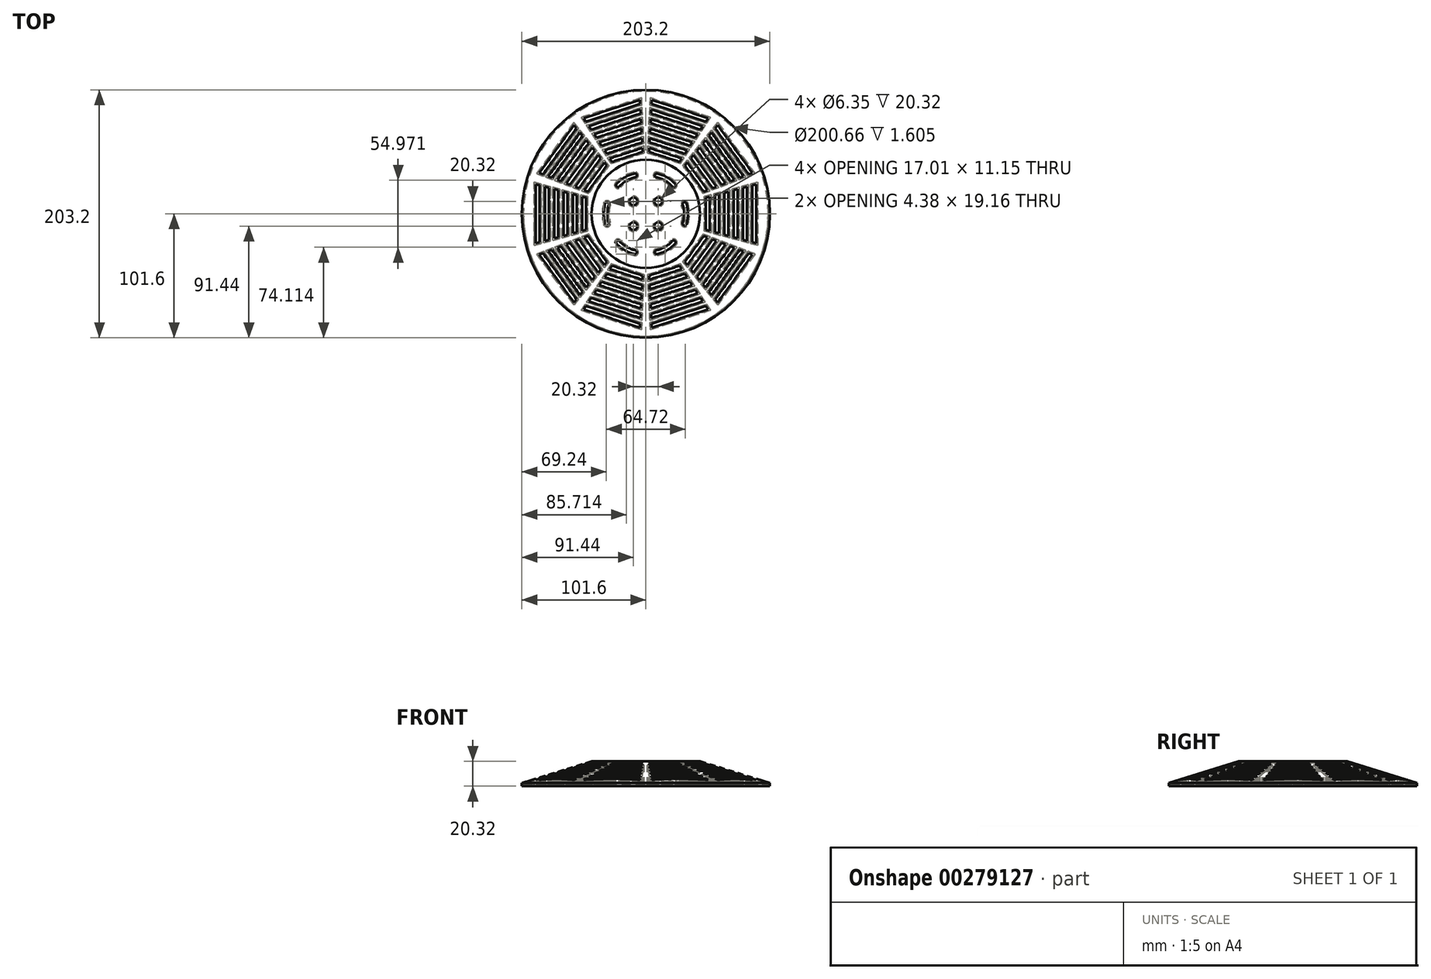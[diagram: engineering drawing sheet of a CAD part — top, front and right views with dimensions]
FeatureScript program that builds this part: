
annotation { "Feature Type Name" : "Feature", "Feature Type Description" : "" }
export const myFeature = defineFeature(function(context is Context, id is Id, definition is map)
    precondition{}
    {
        {
            var Q0;
            Q0=qCreatedBy(makeId("Front.planeOp"),FACE);
            var sketch = newSketch(context, id + "F0", { "sketchPlane" : qUnion([Q0])});
            skLineSegment(sketch, "E0", {"start": v(0, 0) * mm, "end": v(0, 20.32) * mm});
            skLineSegment(sketch, "E1", {"start": v(0, 20.32) * mm, "end": v(44.45, 20.32) * mm});
            skLineSegment(sketch, "E2", {"start": v(44.45, 20.32) * mm, "end": v(101.6, 2.54) * mm});
            skLineSegment(sketch, "E3", {"start": v(101.6, 2.54) * mm, "end": v(101.6, 0) * mm});
            skLineSegment(sketch, "E4", {"start": v(101.6, 0) * mm, "end": v(0, 0) * mm});
            skSolve(sketch);
        }
        {
            var Q0;
            Q0=makeQuery(id+"F0.imprint","IMPRINT",FACE,{"disambiguationData":[TD([[makeQuery(id+"F0.imprint","IMPRINT",EDGE,{"derivedFrom":sQuery(id+"F0.wireOp",EDGE,"E0")}),-1.0]])]});
            var Q1;
            Q1=sQuery(id+"F0.wireOp",EDGE,"E0");
            revolve(context, id + "F1", {"entities" : qUnion([Q0]), "axis" : qUnion([Q1]), "revolveType" : RevolveType.FULL});
        }
        {
            var Q0;
            Q0=makeQuery(id+"F1.opRevolve","SWEPT_FACE",FACE,{"disambiguationData":[OSD([sQuery(id+"F0.wireOp",EDGE,"E1")])]});
            var sketch = newSketch(context, id + "F2", { "sketchPlane" : qUnion([Q0])});
            skArc(sketch, "E5", {"start": v(-30.23, 7.53) * mm, "mid": v(-31.38, 0) * mm, "end": v(-30.23, -7.53) * mm});
            skArc(sketch, "E6.0", {"start": v(-33.27, 8.47) * mm, "mid": v(-34.55, 0) * mm, "end": v(-33.27, -8.47) * mm});
            skArc(sketch, "E7", {"start": v(-33.27, -8.47) * mm, "mid": v(-31.28, -9.52) * mm, "end": v(-30.23, -7.53) * mm});
            skArc(sketch, "E8", {"start": v(-30.23, 7.53) * mm, "mid": v(-31.28, 9.52) * mm, "end": v(-33.27, 8.47) * mm});
            skSolve(sketch);
        }
        {
            var Q0;
            Q0=makeQuery(id+"F2.imprint","IMPRINT",FACE,{"disambiguationData":[TD([[makeQuery(id+"F2.imprint","IMPRINT",EDGE,{"derivedFrom":sQuery(id+"F2.wireOp",EDGE,"E5")}),-1.0]])]});
            extrude(context, id + "F3", {"entities" : qUnion([Q0]), "endBound" : BoundingType.THROUGH_ALL, "oppositeDirection" : true, "depth" : 25.4 * mm});
        }
        {
            var Q0;
            Q0=makeQuery(id+"F3.opExtrude","SWEPT_BODY",BODY,{"disambiguationData":[OSD([sQuery(id+"F2.wireOp",EDGE,"E5"),sQuery(id+"F2.wireOp",EDGE,"E6.0"),sQuery(id+"F2.wireOp",EDGE,"E7"),sQuery(id+"F2.wireOp",EDGE,"E8")])]});
            var Q1;
            Q1=makeQuery(id+"F1.opRevolve","SWEPT_EDGE",EDGE,{"disambiguationData":[OSD([sQuery(id+"F0.wireOp",EDGE,"E2"),sQuery(id+"F0.wireOp",EDGE,"E3")])]});
            circularPattern(context, id + "F4", {"entities" : qUnion([Q0]), "axis" : qUnion([Q1]), "angle" : 360 * degree, "instanceCount" : 6, "equalSpace" : true});
        }
        {
            var Q0;
            Q0=makeQuery(id+"F3.opExtrude","SWEPT_BODY",BODY,{"disambiguationData":[OSD([sQuery(id+"F2.wireOp",EDGE,"E5"),sQuery(id+"F2.wireOp",EDGE,"E6.0"),sQuery(id+"F2.wireOp",EDGE,"E7"),sQuery(id+"F2.wireOp",EDGE,"E8")])]});
            var Q1;
            Q1=makeQuery(id+"F4.opPattern","COPY",BODY,{"derivedFrom":makeQuery(id+"F3.opExtrude","SWEPT_BODY",BODY,{"disambiguationData":[OSD([sQuery(id+"F2.wireOp",EDGE,"E5"),sQuery(id+"F2.wireOp",EDGE,"E6.0"),sQuery(id+"F2.wireOp",EDGE,"E7"),sQuery(id+"F2.wireOp",EDGE,"E8")])]}),"instanceName":"1"});
            var Q2;
            Q2=makeQuery(id+"F4.opPattern","COPY",BODY,{"derivedFrom":makeQuery(id+"F3.opExtrude","SWEPT_BODY",BODY,{"disambiguationData":[OSD([sQuery(id+"F2.wireOp",EDGE,"E5"),sQuery(id+"F2.wireOp",EDGE,"E6.0"),sQuery(id+"F2.wireOp",EDGE,"E7"),sQuery(id+"F2.wireOp",EDGE,"E8")])]}),"instanceName":"2"});
            var Q3;
            Q3=makeQuery(id+"F4.opPattern","COPY",BODY,{"derivedFrom":makeQuery(id+"F3.opExtrude","SWEPT_BODY",BODY,{"disambiguationData":[OSD([sQuery(id+"F2.wireOp",EDGE,"E5"),sQuery(id+"F2.wireOp",EDGE,"E6.0"),sQuery(id+"F2.wireOp",EDGE,"E7"),sQuery(id+"F2.wireOp",EDGE,"E8")])]}),"instanceName":"3"});
            var Q4;
            Q4=makeQuery(id+"F4.opPattern","COPY",BODY,{"derivedFrom":makeQuery(id+"F3.opExtrude","SWEPT_BODY",BODY,{"disambiguationData":[OSD([sQuery(id+"F2.wireOp",EDGE,"E5"),sQuery(id+"F2.wireOp",EDGE,"E6.0"),sQuery(id+"F2.wireOp",EDGE,"E7"),sQuery(id+"F2.wireOp",EDGE,"E8")])]}),"instanceName":"4"});
            var Q5;
            Q5=makeQuery(id+"F4.opPattern","COPY",BODY,{"derivedFrom":makeQuery(id+"F3.opExtrude","SWEPT_BODY",BODY,{"disambiguationData":[OSD([sQuery(id+"F2.wireOp",EDGE,"E5"),sQuery(id+"F2.wireOp",EDGE,"E6.0"),sQuery(id+"F2.wireOp",EDGE,"E7"),sQuery(id+"F2.wireOp",EDGE,"E8")])]}),"instanceName":"5"});
            var Q6;
            Q6=makeQuery(id+"F1.opRevolve","SWEPT_BODY",BODY,{"disambiguationData":[OSD([sQuery(id+"F0.wireOp",EDGE,"E0"),sQuery(id+"F0.wireOp",EDGE,"E1"),sQuery(id+"F0.wireOp",EDGE,"E2"),sQuery(id+"F0.wireOp",EDGE,"E3"),sQuery(id+"F0.wireOp",EDGE,"E4")])]});
            booleanBodies(context, id + "F5", {"operationType" : BooleanOperationType.SUBTRACTION, "tools" : qUnion([Q0, Q1, Q2, Q3, Q4, Q5]), "targets" : qUnion([Q6])});
        }
        {
            var Q0;
            Q0=makeQuery(id+"F1.opRevolve","SWEPT_FACE",FACE,{"disambiguationData":[OSD([sQuery(id+"F0.wireOp",EDGE,"E1")])]});
            var sketch = newSketch(context, id + "F6", { "sketchPlane" : qUnion([Q0])});
            skLineSegment(sketch, "E9", {"start": v(0, 0) * mm, "end": v(-98.14, 26.3) * mm});
            skLineSegment(sketch, "E10", {"start": v(0, 0) * mm, "end": v(-98.14, -26.3) * mm});
            skLineSegment(sketch, "E11", {"start": v(-49.07, -13.15) * mm, "end": v(-49.07, 13.15) * mm});
            skLineSegment(sketch, "E12", {"start": v(-52.24, -14) * mm, "end": v(-52.24, 14) * mm});
            skLineSegment(sketch, "E13", {"start": v(-56.69, -15.19) * mm, "end": v(-56.69, 15.19) * mm});
            skLineSegment(sketch, "E14", {"start": v(-59.86, -16.04) * mm, "end": v(-59.86, 16.04) * mm});
            skLineSegment(sketch, "E15", {"start": v(-64.3, -17.23) * mm, "end": v(-64.3, 17.23) * mm});
            skLineSegment(sketch, "E16", {"start": v(-67.48, -18.08) * mm, "end": v(-67.48, 18.08) * mm});
            skLineSegment(sketch, "E17", {"start": v(-71.93, -19.27) * mm, "end": v(-71.93, 19.27) * mm});
            skLineSegment(sketch, "E18", {"start": v(-75.1, -20.12) * mm, "end": v(-75.1, 20.12) * mm});
            skLineSegment(sketch, "E19", {"start": v(-79.55, -21.32) * mm, "end": v(-79.55, 21.32) * mm});
            skLineSegment(sketch, "E20", {"start": v(-82.72, -22.17) * mm, "end": v(-82.72, 22.17) * mm});
            skLineSegment(sketch, "E21", {"start": v(-87.17, -23.36) * mm, "end": v(-87.17, 23.36) * mm});
            skLineSegment(sketch, "E22", {"start": v(-90.34, -24.2) * mm, "end": v(-90.34, 24.2) * mm});
            skSolve(sketch);
        }
        {
            var Q0;
            {var subQ1=sQuery(id+"F6.wireOp",EDGE,"E19");Q0=makeQuery(id+"F6.imprint","IMPRINT",FACE,{"disambiguationData":[TD([[makeQuery(id+"F6.imprint","IMPRINT",EDGE,{"derivedFrom":subQ1}),1.0]])]});}
            var Q1;
            {var subQ1=sQuery(id+"F6.wireOp",EDGE,"E17");Q1=makeQuery(id+"F6.imprint","IMPRINT",FACE,{"disambiguationData":[TD([[makeQuery(id+"F6.imprint","IMPRINT",EDGE,{"derivedFrom":subQ1}),1.0]])]});}
            var Q2;
            {var subQ1=sQuery(id+"F6.wireOp",EDGE,"E15");Q2=makeQuery(id+"F6.imprint","IMPRINT",FACE,{"disambiguationData":[TD([[makeQuery(id+"F6.imprint","IMPRINT",EDGE,{"derivedFrom":subQ1}),1.0]])]});}
            var Q3;
            {var subQ1=sQuery(id+"F6.wireOp",EDGE,"E13");Q3=makeQuery(id+"F6.imprint","IMPRINT",FACE,{"disambiguationData":[TD([[makeQuery(id+"F6.imprint","IMPRINT",EDGE,{"derivedFrom":subQ1}),1.0]])]});}
            var Q4;
            {var subQ1=sQuery(id+"F6.wireOp",EDGE,"E11");Q4=makeQuery(id+"F6.imprint","IMPRINT",FACE,{"disambiguationData":[TD([[makeQuery(id+"F6.imprint","IMPRINT",EDGE,{"derivedFrom":subQ1}),1.0]])]});}
            var Q5;
            {var subQ1=sQuery(id+"F6.wireOp",EDGE,"E21");Q5=makeQuery(id+"F6.imprint","IMPRINT",FACE,{"disambiguationData":[TD([[makeQuery(id+"F6.imprint","IMPRINT",EDGE,{"derivedFrom":subQ1}),1.0]])]});}
            extrude(context, id + "F7", {"entities" : qUnion([Q0, Q1, Q2, Q3, Q4, Q5]), "oppositeDirection" : true, "depth" : 25.4 * mm});
        }
        {
            var Q0;
            Q0=makeQuery(id+"F7.opExtrude","SWEPT_BODY",BODY,{"disambiguationData":[OSD([sQuery(id+"F6.wireOp",EDGE,"E9"),sQuery(id+"F6.wireOp",EDGE,"E10"),sQuery(id+"F6.wireOp",EDGE,"E21"),sQuery(id+"F6.wireOp",EDGE,"E22")])]});
            var Q1;
            Q1=makeQuery(id+"F7.opExtrude","SWEPT_BODY",BODY,{"disambiguationData":[OSD([sQuery(id+"F6.wireOp",EDGE,"E9"),sQuery(id+"F6.wireOp",EDGE,"E10"),sQuery(id+"F6.wireOp",EDGE,"E19"),sQuery(id+"F6.wireOp",EDGE,"E20")])]});
            var Q2;
            Q2=makeQuery(id+"F7.opExtrude","SWEPT_BODY",BODY,{"disambiguationData":[OSD([sQuery(id+"F6.wireOp",EDGE,"E9"),sQuery(id+"F6.wireOp",EDGE,"E10"),sQuery(id+"F6.wireOp",EDGE,"E17"),sQuery(id+"F6.wireOp",EDGE,"E18")])]});
            var Q3;
            Q3=makeQuery(id+"F7.opExtrude","SWEPT_BODY",BODY,{"disambiguationData":[OSD([sQuery(id+"F6.wireOp",EDGE,"E9"),sQuery(id+"F6.wireOp",EDGE,"E10"),sQuery(id+"F6.wireOp",EDGE,"E15"),sQuery(id+"F6.wireOp",EDGE,"E16")])]});
            var Q4;
            Q4=makeQuery(id+"F7.opExtrude","SWEPT_BODY",BODY,{"disambiguationData":[OSD([sQuery(id+"F6.wireOp",EDGE,"E9"),sQuery(id+"F6.wireOp",EDGE,"E10"),sQuery(id+"F6.wireOp",EDGE,"E13"),sQuery(id+"F6.wireOp",EDGE,"E14")])]});
            var Q5;
            Q5=makeQuery(id+"F7.opExtrude","SWEPT_BODY",BODY,{"disambiguationData":[OSD([sQuery(id+"F6.wireOp",EDGE,"E9"),sQuery(id+"F6.wireOp",EDGE,"E10"),sQuery(id+"F6.wireOp",EDGE,"E11"),sQuery(id+"F6.wireOp",EDGE,"E12")])]});
            var Q6;
            Q6=makeQuery(id+"F1.opRevolve","SWEPT_EDGE",EDGE,{"disambiguationData":[OSD([sQuery(id+"F0.wireOp",EDGE,"E2"),sQuery(id+"F0.wireOp",EDGE,"E3")])]});
            circularPattern(context, id + "F8", {"entities" : qUnion([Q0, Q1, Q2, Q3, Q4, Q5]), "axis" : qUnion([Q6]), "angle" : 360 * degree, "instanceCount" : 10, "equalSpace" : true});
        }
        {
            var Q0;
            Q0=makeQuery(id+"F7.opExtrude","SWEPT_BODY",BODY,{"disambiguationData":[OSD([sQuery(id+"F6.wireOp",EDGE,"E9"),sQuery(id+"F6.wireOp",EDGE,"E10"),sQuery(id+"F6.wireOp",EDGE,"E21"),sQuery(id+"F6.wireOp",EDGE,"E22")])]});
            var Q1;
            Q1=makeQuery(id+"F7.opExtrude","SWEPT_BODY",BODY,{"disambiguationData":[OSD([sQuery(id+"F6.wireOp",EDGE,"E9"),sQuery(id+"F6.wireOp",EDGE,"E10"),sQuery(id+"F6.wireOp",EDGE,"E11"),sQuery(id+"F6.wireOp",EDGE,"E12")])]});
            var Q2;
            Q2=makeQuery(id+"F7.opExtrude","SWEPT_BODY",BODY,{"disambiguationData":[OSD([sQuery(id+"F6.wireOp",EDGE,"E9"),sQuery(id+"F6.wireOp",EDGE,"E10"),sQuery(id+"F6.wireOp",EDGE,"E13"),sQuery(id+"F6.wireOp",EDGE,"E14")])]});
            var Q3;
            Q3=makeQuery(id+"F7.opExtrude","SWEPT_BODY",BODY,{"disambiguationData":[OSD([sQuery(id+"F6.wireOp",EDGE,"E9"),sQuery(id+"F6.wireOp",EDGE,"E10"),sQuery(id+"F6.wireOp",EDGE,"E15"),sQuery(id+"F6.wireOp",EDGE,"E16")])]});
            var Q4;
            Q4=makeQuery(id+"F7.opExtrude","SWEPT_BODY",BODY,{"disambiguationData":[OSD([sQuery(id+"F6.wireOp",EDGE,"E9"),sQuery(id+"F6.wireOp",EDGE,"E10"),sQuery(id+"F6.wireOp",EDGE,"E17"),sQuery(id+"F6.wireOp",EDGE,"E18")])]});
            var Q5;
            Q5=makeQuery(id+"F7.opExtrude","SWEPT_BODY",BODY,{"disambiguationData":[OSD([sQuery(id+"F6.wireOp",EDGE,"E9"),sQuery(id+"F6.wireOp",EDGE,"E10"),sQuery(id+"F6.wireOp",EDGE,"E19"),sQuery(id+"F6.wireOp",EDGE,"E20")])]});
            var Q6;
            Q6=makeQuery(id+"F8.opPattern","COPY",BODY,{"derivedFrom":makeQuery(id+"F7.opExtrude","SWEPT_BODY",BODY,{"disambiguationData":[OSD([sQuery(id+"F6.wireOp",EDGE,"E9"),sQuery(id+"F6.wireOp",EDGE,"E10"),sQuery(id+"F6.wireOp",EDGE,"E21"),sQuery(id+"F6.wireOp",EDGE,"E22")])]}),"instanceName":"1"});
            var Q7;
            Q7=makeQuery(id+"F8.opPattern","COPY",BODY,{"derivedFrom":makeQuery(id+"F7.opExtrude","SWEPT_BODY",BODY,{"disambiguationData":[OSD([sQuery(id+"F6.wireOp",EDGE,"E9"),sQuery(id+"F6.wireOp",EDGE,"E10"),sQuery(id+"F6.wireOp",EDGE,"E11"),sQuery(id+"F6.wireOp",EDGE,"E12")])]}),"instanceName":"1"});
            var Q8;
            Q8=makeQuery(id+"F8.opPattern","COPY",BODY,{"derivedFrom":makeQuery(id+"F7.opExtrude","SWEPT_BODY",BODY,{"disambiguationData":[OSD([sQuery(id+"F6.wireOp",EDGE,"E9"),sQuery(id+"F6.wireOp",EDGE,"E10"),sQuery(id+"F6.wireOp",EDGE,"E13"),sQuery(id+"F6.wireOp",EDGE,"E14")])]}),"instanceName":"1"});
            var Q9;
            Q9=makeQuery(id+"F8.opPattern","COPY",BODY,{"derivedFrom":makeQuery(id+"F7.opExtrude","SWEPT_BODY",BODY,{"disambiguationData":[OSD([sQuery(id+"F6.wireOp",EDGE,"E9"),sQuery(id+"F6.wireOp",EDGE,"E10"),sQuery(id+"F6.wireOp",EDGE,"E15"),sQuery(id+"F6.wireOp",EDGE,"E16")])]}),"instanceName":"1"});
            var Q10;
            Q10=makeQuery(id+"F8.opPattern","COPY",BODY,{"derivedFrom":makeQuery(id+"F7.opExtrude","SWEPT_BODY",BODY,{"disambiguationData":[OSD([sQuery(id+"F6.wireOp",EDGE,"E9"),sQuery(id+"F6.wireOp",EDGE,"E10"),sQuery(id+"F6.wireOp",EDGE,"E17"),sQuery(id+"F6.wireOp",EDGE,"E18")])]}),"instanceName":"1"});
            var Q11;
            Q11=makeQuery(id+"F8.opPattern","COPY",BODY,{"derivedFrom":makeQuery(id+"F7.opExtrude","SWEPT_BODY",BODY,{"disambiguationData":[OSD([sQuery(id+"F6.wireOp",EDGE,"E9"),sQuery(id+"F6.wireOp",EDGE,"E10"),sQuery(id+"F6.wireOp",EDGE,"E19"),sQuery(id+"F6.wireOp",EDGE,"E20")])]}),"instanceName":"1"});
            var Q12;
            Q12=makeQuery(id+"F8.opPattern","COPY",BODY,{"derivedFrom":makeQuery(id+"F7.opExtrude","SWEPT_BODY",BODY,{"disambiguationData":[OSD([sQuery(id+"F6.wireOp",EDGE,"E9"),sQuery(id+"F6.wireOp",EDGE,"E10"),sQuery(id+"F6.wireOp",EDGE,"E21"),sQuery(id+"F6.wireOp",EDGE,"E22")])]}),"instanceName":"2"});
            var Q13;
            Q13=makeQuery(id+"F8.opPattern","COPY",BODY,{"derivedFrom":makeQuery(id+"F7.opExtrude","SWEPT_BODY",BODY,{"disambiguationData":[OSD([sQuery(id+"F6.wireOp",EDGE,"E9"),sQuery(id+"F6.wireOp",EDGE,"E10"),sQuery(id+"F6.wireOp",EDGE,"E11"),sQuery(id+"F6.wireOp",EDGE,"E12")])]}),"instanceName":"2"});
            var Q14;
            Q14=makeQuery(id+"F8.opPattern","COPY",BODY,{"derivedFrom":makeQuery(id+"F7.opExtrude","SWEPT_BODY",BODY,{"disambiguationData":[OSD([sQuery(id+"F6.wireOp",EDGE,"E9"),sQuery(id+"F6.wireOp",EDGE,"E10"),sQuery(id+"F6.wireOp",EDGE,"E13"),sQuery(id+"F6.wireOp",EDGE,"E14")])]}),"instanceName":"2"});
            var Q15;
            Q15=makeQuery(id+"F8.opPattern","COPY",BODY,{"derivedFrom":makeQuery(id+"F7.opExtrude","SWEPT_BODY",BODY,{"disambiguationData":[OSD([sQuery(id+"F6.wireOp",EDGE,"E9"),sQuery(id+"F6.wireOp",EDGE,"E10"),sQuery(id+"F6.wireOp",EDGE,"E15"),sQuery(id+"F6.wireOp",EDGE,"E16")])]}),"instanceName":"2"});
            var Q16;
            Q16=makeQuery(id+"F8.opPattern","COPY",BODY,{"derivedFrom":makeQuery(id+"F7.opExtrude","SWEPT_BODY",BODY,{"disambiguationData":[OSD([sQuery(id+"F6.wireOp",EDGE,"E9"),sQuery(id+"F6.wireOp",EDGE,"E10"),sQuery(id+"F6.wireOp",EDGE,"E17"),sQuery(id+"F6.wireOp",EDGE,"E18")])]}),"instanceName":"2"});
            var Q17;
            Q17=makeQuery(id+"F8.opPattern","COPY",BODY,{"derivedFrom":makeQuery(id+"F7.opExtrude","SWEPT_BODY",BODY,{"disambiguationData":[OSD([sQuery(id+"F6.wireOp",EDGE,"E9"),sQuery(id+"F6.wireOp",EDGE,"E10"),sQuery(id+"F6.wireOp",EDGE,"E19"),sQuery(id+"F6.wireOp",EDGE,"E20")])]}),"instanceName":"2"});
            var Q18;
            Q18=makeQuery(id+"F8.opPattern","COPY",BODY,{"derivedFrom":makeQuery(id+"F7.opExtrude","SWEPT_BODY",BODY,{"disambiguationData":[OSD([sQuery(id+"F6.wireOp",EDGE,"E9"),sQuery(id+"F6.wireOp",EDGE,"E10"),sQuery(id+"F6.wireOp",EDGE,"E21"),sQuery(id+"F6.wireOp",EDGE,"E22")])]}),"instanceName":"3"});
            var Q19;
            Q19=makeQuery(id+"F8.opPattern","COPY",BODY,{"derivedFrom":makeQuery(id+"F7.opExtrude","SWEPT_BODY",BODY,{"disambiguationData":[OSD([sQuery(id+"F6.wireOp",EDGE,"E9"),sQuery(id+"F6.wireOp",EDGE,"E10"),sQuery(id+"F6.wireOp",EDGE,"E11"),sQuery(id+"F6.wireOp",EDGE,"E12")])]}),"instanceName":"3"});
            var Q20;
            Q20=makeQuery(id+"F8.opPattern","COPY",BODY,{"derivedFrom":makeQuery(id+"F7.opExtrude","SWEPT_BODY",BODY,{"disambiguationData":[OSD([sQuery(id+"F6.wireOp",EDGE,"E9"),sQuery(id+"F6.wireOp",EDGE,"E10"),sQuery(id+"F6.wireOp",EDGE,"E13"),sQuery(id+"F6.wireOp",EDGE,"E14")])]}),"instanceName":"3"});
            var Q21;
            Q21=makeQuery(id+"F8.opPattern","COPY",BODY,{"derivedFrom":makeQuery(id+"F7.opExtrude","SWEPT_BODY",BODY,{"disambiguationData":[OSD([sQuery(id+"F6.wireOp",EDGE,"E9"),sQuery(id+"F6.wireOp",EDGE,"E10"),sQuery(id+"F6.wireOp",EDGE,"E15"),sQuery(id+"F6.wireOp",EDGE,"E16")])]}),"instanceName":"3"});
            var Q22;
            Q22=makeQuery(id+"F8.opPattern","COPY",BODY,{"derivedFrom":makeQuery(id+"F7.opExtrude","SWEPT_BODY",BODY,{"disambiguationData":[OSD([sQuery(id+"F6.wireOp",EDGE,"E9"),sQuery(id+"F6.wireOp",EDGE,"E10"),sQuery(id+"F6.wireOp",EDGE,"E17"),sQuery(id+"F6.wireOp",EDGE,"E18")])]}),"instanceName":"3"});
            var Q23;
            Q23=makeQuery(id+"F8.opPattern","COPY",BODY,{"derivedFrom":makeQuery(id+"F7.opExtrude","SWEPT_BODY",BODY,{"disambiguationData":[OSD([sQuery(id+"F6.wireOp",EDGE,"E9"),sQuery(id+"F6.wireOp",EDGE,"E10"),sQuery(id+"F6.wireOp",EDGE,"E19"),sQuery(id+"F6.wireOp",EDGE,"E20")])]}),"instanceName":"3"});
            var Q24;
            Q24=makeQuery(id+"F8.opPattern","COPY",BODY,{"derivedFrom":makeQuery(id+"F7.opExtrude","SWEPT_BODY",BODY,{"disambiguationData":[OSD([sQuery(id+"F6.wireOp",EDGE,"E9"),sQuery(id+"F6.wireOp",EDGE,"E10"),sQuery(id+"F6.wireOp",EDGE,"E21"),sQuery(id+"F6.wireOp",EDGE,"E22")])]}),"instanceName":"4"});
            var Q25;
            Q25=makeQuery(id+"F8.opPattern","COPY",BODY,{"derivedFrom":makeQuery(id+"F7.opExtrude","SWEPT_BODY",BODY,{"disambiguationData":[OSD([sQuery(id+"F6.wireOp",EDGE,"E9"),sQuery(id+"F6.wireOp",EDGE,"E10"),sQuery(id+"F6.wireOp",EDGE,"E11"),sQuery(id+"F6.wireOp",EDGE,"E12")])]}),"instanceName":"4"});
            var Q26;
            Q26=makeQuery(id+"F8.opPattern","COPY",BODY,{"derivedFrom":makeQuery(id+"F7.opExtrude","SWEPT_BODY",BODY,{"disambiguationData":[OSD([sQuery(id+"F6.wireOp",EDGE,"E9"),sQuery(id+"F6.wireOp",EDGE,"E10"),sQuery(id+"F6.wireOp",EDGE,"E13"),sQuery(id+"F6.wireOp",EDGE,"E14")])]}),"instanceName":"4"});
            var Q27;
            Q27=makeQuery(id+"F8.opPattern","COPY",BODY,{"derivedFrom":makeQuery(id+"F7.opExtrude","SWEPT_BODY",BODY,{"disambiguationData":[OSD([sQuery(id+"F6.wireOp",EDGE,"E9"),sQuery(id+"F6.wireOp",EDGE,"E10"),sQuery(id+"F6.wireOp",EDGE,"E15"),sQuery(id+"F6.wireOp",EDGE,"E16")])]}),"instanceName":"4"});
            var Q28;
            Q28=makeQuery(id+"F8.opPattern","COPY",BODY,{"derivedFrom":makeQuery(id+"F7.opExtrude","SWEPT_BODY",BODY,{"disambiguationData":[OSD([sQuery(id+"F6.wireOp",EDGE,"E9"),sQuery(id+"F6.wireOp",EDGE,"E10"),sQuery(id+"F6.wireOp",EDGE,"E17"),sQuery(id+"F6.wireOp",EDGE,"E18")])]}),"instanceName":"4"});
            var Q29;
            Q29=makeQuery(id+"F8.opPattern","COPY",BODY,{"derivedFrom":makeQuery(id+"F7.opExtrude","SWEPT_BODY",BODY,{"disambiguationData":[OSD([sQuery(id+"F6.wireOp",EDGE,"E9"),sQuery(id+"F6.wireOp",EDGE,"E10"),sQuery(id+"F6.wireOp",EDGE,"E19"),sQuery(id+"F6.wireOp",EDGE,"E20")])]}),"instanceName":"4"});
            var Q30;
            Q30=makeQuery(id+"F8.opPattern","COPY",BODY,{"derivedFrom":makeQuery(id+"F7.opExtrude","SWEPT_BODY",BODY,{"disambiguationData":[OSD([sQuery(id+"F6.wireOp",EDGE,"E9"),sQuery(id+"F6.wireOp",EDGE,"E10"),sQuery(id+"F6.wireOp",EDGE,"E21"),sQuery(id+"F6.wireOp",EDGE,"E22")])]}),"instanceName":"5"});
            var Q31;
            Q31=makeQuery(id+"F8.opPattern","COPY",BODY,{"derivedFrom":makeQuery(id+"F7.opExtrude","SWEPT_BODY",BODY,{"disambiguationData":[OSD([sQuery(id+"F6.wireOp",EDGE,"E9"),sQuery(id+"F6.wireOp",EDGE,"E10"),sQuery(id+"F6.wireOp",EDGE,"E11"),sQuery(id+"F6.wireOp",EDGE,"E12")])]}),"instanceName":"5"});
            var Q32;
            Q32=makeQuery(id+"F8.opPattern","COPY",BODY,{"derivedFrom":makeQuery(id+"F7.opExtrude","SWEPT_BODY",BODY,{"disambiguationData":[OSD([sQuery(id+"F6.wireOp",EDGE,"E9"),sQuery(id+"F6.wireOp",EDGE,"E10"),sQuery(id+"F6.wireOp",EDGE,"E13"),sQuery(id+"F6.wireOp",EDGE,"E14")])]}),"instanceName":"5"});
            var Q33;
            Q33=makeQuery(id+"F8.opPattern","COPY",BODY,{"derivedFrom":makeQuery(id+"F7.opExtrude","SWEPT_BODY",BODY,{"disambiguationData":[OSD([sQuery(id+"F6.wireOp",EDGE,"E9"),sQuery(id+"F6.wireOp",EDGE,"E10"),sQuery(id+"F6.wireOp",EDGE,"E15"),sQuery(id+"F6.wireOp",EDGE,"E16")])]}),"instanceName":"5"});
            var Q34;
            Q34=makeQuery(id+"F8.opPattern","COPY",BODY,{"derivedFrom":makeQuery(id+"F7.opExtrude","SWEPT_BODY",BODY,{"disambiguationData":[OSD([sQuery(id+"F6.wireOp",EDGE,"E9"),sQuery(id+"F6.wireOp",EDGE,"E10"),sQuery(id+"F6.wireOp",EDGE,"E17"),sQuery(id+"F6.wireOp",EDGE,"E18")])]}),"instanceName":"5"});
            var Q35;
            Q35=makeQuery(id+"F8.opPattern","COPY",BODY,{"derivedFrom":makeQuery(id+"F7.opExtrude","SWEPT_BODY",BODY,{"disambiguationData":[OSD([sQuery(id+"F6.wireOp",EDGE,"E9"),sQuery(id+"F6.wireOp",EDGE,"E10"),sQuery(id+"F6.wireOp",EDGE,"E19"),sQuery(id+"F6.wireOp",EDGE,"E20")])]}),"instanceName":"5"});
            var Q36;
            Q36=makeQuery(id+"F8.opPattern","COPY",BODY,{"derivedFrom":makeQuery(id+"F7.opExtrude","SWEPT_BODY",BODY,{"disambiguationData":[OSD([sQuery(id+"F6.wireOp",EDGE,"E9"),sQuery(id+"F6.wireOp",EDGE,"E10"),sQuery(id+"F6.wireOp",EDGE,"E21"),sQuery(id+"F6.wireOp",EDGE,"E22")])]}),"instanceName":"6"});
            var Q37;
            Q37=makeQuery(id+"F8.opPattern","COPY",BODY,{"derivedFrom":makeQuery(id+"F7.opExtrude","SWEPT_BODY",BODY,{"disambiguationData":[OSD([sQuery(id+"F6.wireOp",EDGE,"E9"),sQuery(id+"F6.wireOp",EDGE,"E10"),sQuery(id+"F6.wireOp",EDGE,"E11"),sQuery(id+"F6.wireOp",EDGE,"E12")])]}),"instanceName":"6"});
            var Q38;
            Q38=makeQuery(id+"F8.opPattern","COPY",BODY,{"derivedFrom":makeQuery(id+"F7.opExtrude","SWEPT_BODY",BODY,{"disambiguationData":[OSD([sQuery(id+"F6.wireOp",EDGE,"E9"),sQuery(id+"F6.wireOp",EDGE,"E10"),sQuery(id+"F6.wireOp",EDGE,"E13"),sQuery(id+"F6.wireOp",EDGE,"E14")])]}),"instanceName":"6"});
            var Q39;
            Q39=makeQuery(id+"F8.opPattern","COPY",BODY,{"derivedFrom":makeQuery(id+"F7.opExtrude","SWEPT_BODY",BODY,{"disambiguationData":[OSD([sQuery(id+"F6.wireOp",EDGE,"E9"),sQuery(id+"F6.wireOp",EDGE,"E10"),sQuery(id+"F6.wireOp",EDGE,"E15"),sQuery(id+"F6.wireOp",EDGE,"E16")])]}),"instanceName":"6"});
            var Q40;
            Q40=makeQuery(id+"F8.opPattern","COPY",BODY,{"derivedFrom":makeQuery(id+"F7.opExtrude","SWEPT_BODY",BODY,{"disambiguationData":[OSD([sQuery(id+"F6.wireOp",EDGE,"E9"),sQuery(id+"F6.wireOp",EDGE,"E10"),sQuery(id+"F6.wireOp",EDGE,"E17"),sQuery(id+"F6.wireOp",EDGE,"E18")])]}),"instanceName":"6"});
            var Q41;
            Q41=makeQuery(id+"F8.opPattern","COPY",BODY,{"derivedFrom":makeQuery(id+"F7.opExtrude","SWEPT_BODY",BODY,{"disambiguationData":[OSD([sQuery(id+"F6.wireOp",EDGE,"E9"),sQuery(id+"F6.wireOp",EDGE,"E10"),sQuery(id+"F6.wireOp",EDGE,"E19"),sQuery(id+"F6.wireOp",EDGE,"E20")])]}),"instanceName":"6"});
            var Q42;
            Q42=makeQuery(id+"F8.opPattern","COPY",BODY,{"derivedFrom":makeQuery(id+"F7.opExtrude","SWEPT_BODY",BODY,{"disambiguationData":[OSD([sQuery(id+"F6.wireOp",EDGE,"E9"),sQuery(id+"F6.wireOp",EDGE,"E10"),sQuery(id+"F6.wireOp",EDGE,"E21"),sQuery(id+"F6.wireOp",EDGE,"E22")])]}),"instanceName":"7"});
            var Q43;
            Q43=makeQuery(id+"F8.opPattern","COPY",BODY,{"derivedFrom":makeQuery(id+"F7.opExtrude","SWEPT_BODY",BODY,{"disambiguationData":[OSD([sQuery(id+"F6.wireOp",EDGE,"E9"),sQuery(id+"F6.wireOp",EDGE,"E10"),sQuery(id+"F6.wireOp",EDGE,"E11"),sQuery(id+"F6.wireOp",EDGE,"E12")])]}),"instanceName":"7"});
            var Q44;
            Q44=makeQuery(id+"F8.opPattern","COPY",BODY,{"derivedFrom":makeQuery(id+"F7.opExtrude","SWEPT_BODY",BODY,{"disambiguationData":[OSD([sQuery(id+"F6.wireOp",EDGE,"E9"),sQuery(id+"F6.wireOp",EDGE,"E10"),sQuery(id+"F6.wireOp",EDGE,"E13"),sQuery(id+"F6.wireOp",EDGE,"E14")])]}),"instanceName":"7"});
            var Q45;
            Q45=makeQuery(id+"F8.opPattern","COPY",BODY,{"derivedFrom":makeQuery(id+"F7.opExtrude","SWEPT_BODY",BODY,{"disambiguationData":[OSD([sQuery(id+"F6.wireOp",EDGE,"E9"),sQuery(id+"F6.wireOp",EDGE,"E10"),sQuery(id+"F6.wireOp",EDGE,"E15"),sQuery(id+"F6.wireOp",EDGE,"E16")])]}),"instanceName":"7"});
            var Q46;
            Q46=makeQuery(id+"F8.opPattern","COPY",BODY,{"derivedFrom":makeQuery(id+"F7.opExtrude","SWEPT_BODY",BODY,{"disambiguationData":[OSD([sQuery(id+"F6.wireOp",EDGE,"E9"),sQuery(id+"F6.wireOp",EDGE,"E10"),sQuery(id+"F6.wireOp",EDGE,"E17"),sQuery(id+"F6.wireOp",EDGE,"E18")])]}),"instanceName":"7"});
            var Q47;
            Q47=makeQuery(id+"F8.opPattern","COPY",BODY,{"derivedFrom":makeQuery(id+"F7.opExtrude","SWEPT_BODY",BODY,{"disambiguationData":[OSD([sQuery(id+"F6.wireOp",EDGE,"E9"),sQuery(id+"F6.wireOp",EDGE,"E10"),sQuery(id+"F6.wireOp",EDGE,"E19"),sQuery(id+"F6.wireOp",EDGE,"E20")])]}),"instanceName":"7"});
            var Q48;
            Q48=makeQuery(id+"F8.opPattern","COPY",BODY,{"derivedFrom":makeQuery(id+"F7.opExtrude","SWEPT_BODY",BODY,{"disambiguationData":[OSD([sQuery(id+"F6.wireOp",EDGE,"E9"),sQuery(id+"F6.wireOp",EDGE,"E10"),sQuery(id+"F6.wireOp",EDGE,"E21"),sQuery(id+"F6.wireOp",EDGE,"E22")])]}),"instanceName":"8"});
            var Q49;
            Q49=makeQuery(id+"F8.opPattern","COPY",BODY,{"derivedFrom":makeQuery(id+"F7.opExtrude","SWEPT_BODY",BODY,{"disambiguationData":[OSD([sQuery(id+"F6.wireOp",EDGE,"E9"),sQuery(id+"F6.wireOp",EDGE,"E10"),sQuery(id+"F6.wireOp",EDGE,"E11"),sQuery(id+"F6.wireOp",EDGE,"E12")])]}),"instanceName":"8"});
            var Q50;
            Q50=makeQuery(id+"F8.opPattern","COPY",BODY,{"derivedFrom":makeQuery(id+"F7.opExtrude","SWEPT_BODY",BODY,{"disambiguationData":[OSD([sQuery(id+"F6.wireOp",EDGE,"E9"),sQuery(id+"F6.wireOp",EDGE,"E10"),sQuery(id+"F6.wireOp",EDGE,"E13"),sQuery(id+"F6.wireOp",EDGE,"E14")])]}),"instanceName":"8"});
            var Q51;
            Q51=makeQuery(id+"F8.opPattern","COPY",BODY,{"derivedFrom":makeQuery(id+"F7.opExtrude","SWEPT_BODY",BODY,{"disambiguationData":[OSD([sQuery(id+"F6.wireOp",EDGE,"E9"),sQuery(id+"F6.wireOp",EDGE,"E10"),sQuery(id+"F6.wireOp",EDGE,"E15"),sQuery(id+"F6.wireOp",EDGE,"E16")])]}),"instanceName":"8"});
            var Q52;
            Q52=makeQuery(id+"F8.opPattern","COPY",BODY,{"derivedFrom":makeQuery(id+"F7.opExtrude","SWEPT_BODY",BODY,{"disambiguationData":[OSD([sQuery(id+"F6.wireOp",EDGE,"E9"),sQuery(id+"F6.wireOp",EDGE,"E10"),sQuery(id+"F6.wireOp",EDGE,"E17"),sQuery(id+"F6.wireOp",EDGE,"E18")])]}),"instanceName":"8"});
            var Q53;
            Q53=makeQuery(id+"F8.opPattern","COPY",BODY,{"derivedFrom":makeQuery(id+"F7.opExtrude","SWEPT_BODY",BODY,{"disambiguationData":[OSD([sQuery(id+"F6.wireOp",EDGE,"E9"),sQuery(id+"F6.wireOp",EDGE,"E10"),sQuery(id+"F6.wireOp",EDGE,"E19"),sQuery(id+"F6.wireOp",EDGE,"E20")])]}),"instanceName":"8"});
            var Q54;
            Q54=makeQuery(id+"F8.opPattern","COPY",BODY,{"derivedFrom":makeQuery(id+"F7.opExtrude","SWEPT_BODY",BODY,{"disambiguationData":[OSD([sQuery(id+"F6.wireOp",EDGE,"E9"),sQuery(id+"F6.wireOp",EDGE,"E10"),sQuery(id+"F6.wireOp",EDGE,"E21"),sQuery(id+"F6.wireOp",EDGE,"E22")])]}),"instanceName":"9"});
            var Q55;
            Q55=makeQuery(id+"F8.opPattern","COPY",BODY,{"derivedFrom":makeQuery(id+"F7.opExtrude","SWEPT_BODY",BODY,{"disambiguationData":[OSD([sQuery(id+"F6.wireOp",EDGE,"E9"),sQuery(id+"F6.wireOp",EDGE,"E10"),sQuery(id+"F6.wireOp",EDGE,"E11"),sQuery(id+"F6.wireOp",EDGE,"E12")])]}),"instanceName":"9"});
            var Q56;
            Q56=makeQuery(id+"F8.opPattern","COPY",BODY,{"derivedFrom":makeQuery(id+"F7.opExtrude","SWEPT_BODY",BODY,{"disambiguationData":[OSD([sQuery(id+"F6.wireOp",EDGE,"E9"),sQuery(id+"F6.wireOp",EDGE,"E10"),sQuery(id+"F6.wireOp",EDGE,"E13"),sQuery(id+"F6.wireOp",EDGE,"E14")])]}),"instanceName":"9"});
            var Q57;
            Q57=makeQuery(id+"F8.opPattern","COPY",BODY,{"derivedFrom":makeQuery(id+"F7.opExtrude","SWEPT_BODY",BODY,{"disambiguationData":[OSD([sQuery(id+"F6.wireOp",EDGE,"E9"),sQuery(id+"F6.wireOp",EDGE,"E10"),sQuery(id+"F6.wireOp",EDGE,"E15"),sQuery(id+"F6.wireOp",EDGE,"E16")])]}),"instanceName":"9"});
            var Q58;
            Q58=makeQuery(id+"F8.opPattern","COPY",BODY,{"derivedFrom":makeQuery(id+"F7.opExtrude","SWEPT_BODY",BODY,{"disambiguationData":[OSD([sQuery(id+"F6.wireOp",EDGE,"E9"),sQuery(id+"F6.wireOp",EDGE,"E10"),sQuery(id+"F6.wireOp",EDGE,"E17"),sQuery(id+"F6.wireOp",EDGE,"E18")])]}),"instanceName":"9"});
            var Q59;
            Q59=makeQuery(id+"F8.opPattern","COPY",BODY,{"derivedFrom":makeQuery(id+"F7.opExtrude","SWEPT_BODY",BODY,{"disambiguationData":[OSD([sQuery(id+"F6.wireOp",EDGE,"E9"),sQuery(id+"F6.wireOp",EDGE,"E10"),sQuery(id+"F6.wireOp",EDGE,"E19"),sQuery(id+"F6.wireOp",EDGE,"E20")])]}),"instanceName":"9"});
            var Q60;
            Q60=makeQuery(id+"F1.opRevolve","SWEPT_BODY",BODY,{"disambiguationData":[OSD([sQuery(id+"F0.wireOp",EDGE,"E0"),sQuery(id+"F0.wireOp",EDGE,"E1"),sQuery(id+"F0.wireOp",EDGE,"E2"),sQuery(id+"F0.wireOp",EDGE,"E3"),sQuery(id+"F0.wireOp",EDGE,"E4")])]});
            booleanBodies(context, id + "F9", {"operationType" : BooleanOperationType.SUBTRACTION, "tools" : qUnion([Q0, Q1, Q2, Q3, Q4, Q5, Q6, Q7, Q8, Q9, Q10, Q11, Q12, Q13, Q14, Q15, Q16, Q17, Q18, Q19, Q20, Q21, Q22, Q23, Q24, Q25, Q26, Q27, Q28, Q29, Q30, Q31, Q32, Q33, Q34, Q35, Q36, Q37, Q38, Q39, Q40, Q41, Q42, Q43, Q44, Q45, Q46, Q47, Q48, Q49, Q50, Q51, Q52, Q53, Q54, Q55, Q56, Q57, Q58, Q59]), "targets" : qUnion([Q60])});
        }
        {
            var Q0;
            Q0=makeQuery(id+"F1.opRevolve","SWEPT_FACE",FACE,{"disambiguationData":[OSD([sQuery(id+"F0.wireOp",EDGE,"E1")])]});
            var sketch = newSketch(context, id + "F10", { "sketchPlane" : qUnion([Q0])});
            skCircle(sketch, "E23", {"center": v(-10.16, -10.16) * mm, "radius": 3.18 * mm});
            skCircle(sketch, "E24", {"center": v(-10.16, 10.16) * mm, "radius": 3.18 * mm});
            skCircle(sketch, "E25", {"center": v(10.16, -10.16) * mm, "radius": 3.18 * mm});
            skCircle(sketch, "E26", {"center": v(10.16, 10.16) * mm, "radius": 3.18 * mm});
            skSolve(sketch);
        }
        {
            var Q0;
            {Q0=qUnion([makeQuery(id+"F10.imprint","IMPRINT",FACE,{"disambiguationData":[TD([[makeQuery(id+"F10.imprint","IMPRINT",EDGE,{"derivedFrom":sQuery(id+"F10.wireOp",EDGE,"E23")}),1.0]])]}),makeQuery(id+"F10.imprint","IMPRINT",FACE,{"disambiguationData":[TD([[makeQuery(id+"F10.imprint","IMPRINT",EDGE,{"derivedFrom":sQuery(id+"F10.wireOp",EDGE,"E24")}),1.0]])]}),makeQuery(id+"F10.imprint","IMPRINT",FACE,{"disambiguationData":[TD([[makeQuery(id+"F10.imprint","IMPRINT",EDGE,{"derivedFrom":sQuery(id+"F10.wireOp",EDGE,"E25")}),1.0]])]}),makeQuery(id+"F10.imprint","IMPRINT",FACE,{"disambiguationData":[TD([[makeQuery(id+"F10.imprint","IMPRINT",EDGE,{"derivedFrom":sQuery(id+"F10.wireOp",EDGE,"E26")}),1.0]])]})]);}
            extrude(context, id + "F11", {"entities" : qUnion([Q0]), "operationType" : NewBodyOperationType.REMOVE, "endBound" : BoundingType.THROUGH_ALL, "oppositeDirection" : true, "depth" : 25.4 * mm});
        }
        {
            var Q0;
            Q0=makeQuery(id+"F1.opRevolve","SWEPT_FACE",FACE,{"disambiguationData":[OSD([sQuery(id+"F0.wireOp",EDGE,"E4")])]});
            shell(context, id + "F12", {"entities" : qUnion([Q0]), "thickness" : 1.27 * mm});
        }
    });
